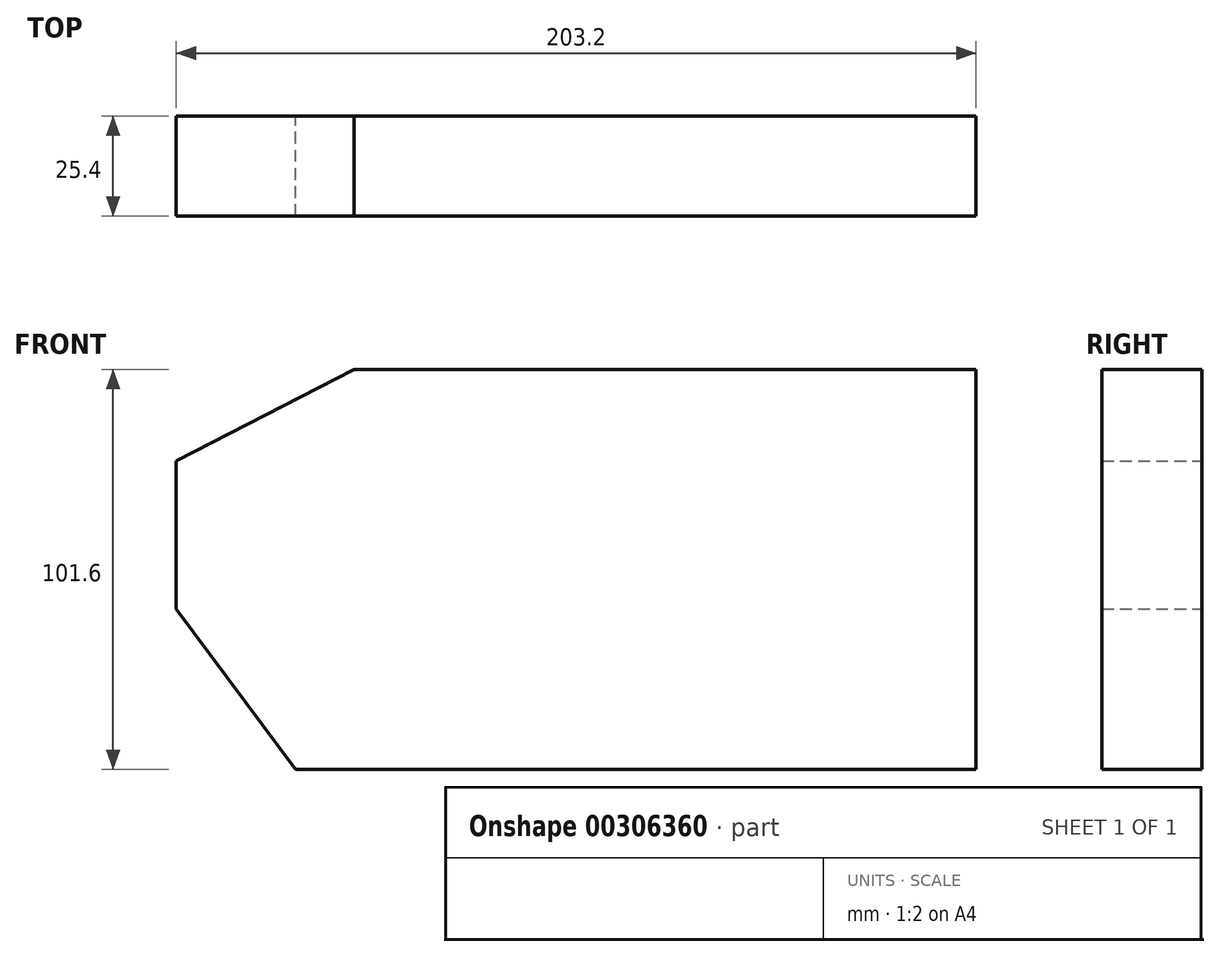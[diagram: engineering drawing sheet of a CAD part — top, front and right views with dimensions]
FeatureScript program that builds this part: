
annotation { "Feature Type Name" : "Feature", "Feature Type Description" : "" }
export const myFeature = defineFeature(function(context is Context, id is Id, definition is map)
    precondition{}
    {
        {
            var Q0;
            Q0=qCreatedBy(makeId("Front.planeOp"),FACE);
            var sketch = newSketch(context, id + "F0", { "sketchPlane" : qUnion([Q0])});
            skLineSegment(sketch, "E0.bottom", {"start": v(-101.6, 50.8) * mm, "end": v(101.6, 50.8) * mm});
            skLineSegment(sketch, "E0.top", {"start": v(-101.6, -50.8) * mm, "end": v(101.6, -50.8) * mm});
            skLineSegment(sketch, "E0.left", {"start": v(-101.6, 50.8) * mm, "end": v(-101.6, -50.8) * mm});
            skLineSegment(sketch, "E0.right", {"start": v(101.6, 50.8) * mm, "end": v(101.6, -50.8) * mm});
            skPoint(sketch, "E0.middle", {"position": v(0, 0) * mm});
            skLineSegment(sketch, "E1", {"start": v(-56.42, 50.8) * mm, "end": v(-101.6, 27.57) * mm});
            skLineSegment(sketch, "E2", {"start": v(-101.6, -10.04) * mm, "end": v(-71.28, -50.8) * mm});
            skSolve(sketch);
        }
        {
            var Q0;
            {var subQ0=sQuery(id+"F0.wireOp",EDGE,"E0.right");Q0=makeQuery(id+"F0.imprint","IMPRINT",FACE,{"disambiguationData":[TD([[makeQuery(id+"F0.imprint","IMPRINT",EDGE,{"derivedFrom":subQ0}),-1.0]])]});}
            extrude(context, id + "F1", {"entities" : qUnion([Q0]), "depth" : 25.4 * mm});
        }
    });
